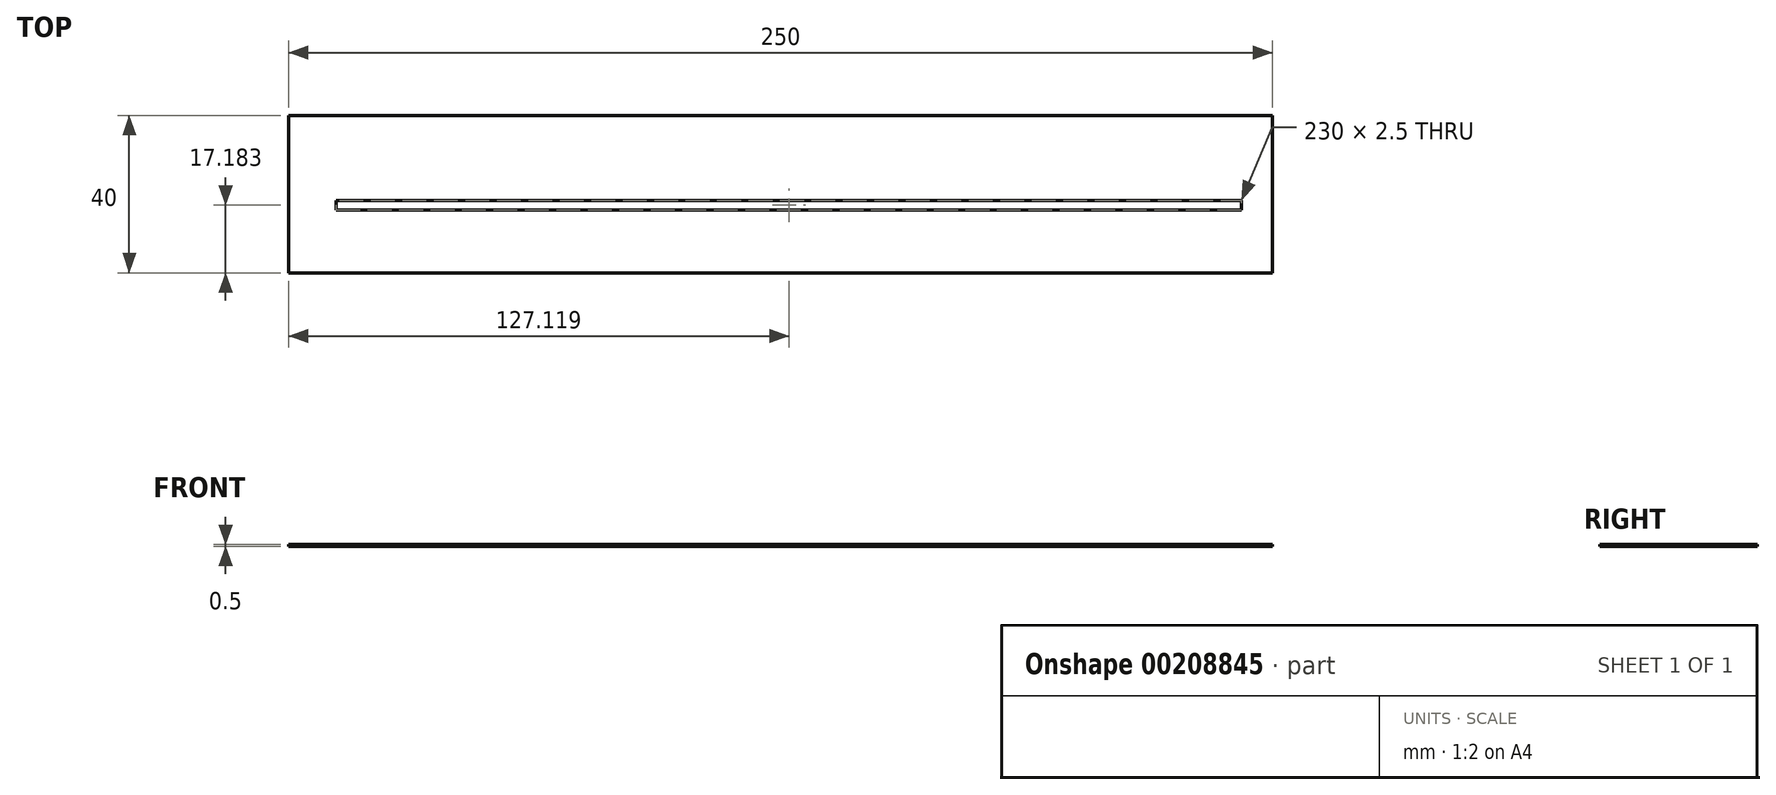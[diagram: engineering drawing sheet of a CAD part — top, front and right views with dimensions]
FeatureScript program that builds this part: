
annotation { "Feature Type Name" : "Feature", "Feature Type Description" : "" }
export const myFeature = defineFeature(function(context is Context, id is Id, definition is map)
    precondition{}
    {
        {
            var Q0;
            Q0=qCreatedBy(makeId("Top.planeOp"),FACE);
            var sketch = newSketch(context, id + "F0", { "sketchPlane" : qUnion([Q0])});
            skLineSegment(sketch, "E0.bottom", {"start": v(-125.07, 12.47) * mm, "end": v(124.93, 12.47) * mm});
            skLineSegment(sketch, "E0.top", {"start": v(-125.07, -27.53) * mm, "end": v(124.93, -27.53) * mm});
            skLineSegment(sketch, "E0.left", {"start": v(-125.07, 12.47) * mm, "end": v(-125.07, -27.53) * mm});
            skLineSegment(sketch, "E0.right", {"start": v(124.93, 12.47) * mm, "end": v(124.93, -27.53) * mm});
            skLineSegment(sketch, "E1.bottom", {"start": v(-112.95, -9.1) * mm, "end": v(117.05, -9.1) * mm});
            skLineSegment(sketch, "E1.top", {"start": v(-112.95, -11.6) * mm, "end": v(117.05, -11.6) * mm});
            skLineSegment(sketch, "E1.left", {"start": v(-112.95, -9.1) * mm, "end": v(-112.95, -11.6) * mm});
            skLineSegment(sketch, "E1.right", {"start": v(117.05, -9.1) * mm, "end": v(117.05, -11.6) * mm});
            skSolve(sketch);
        }
        {
            var Q0;
            Q0=makeQuery(id+"F0.imprint","IMPRINT",FACE,{"disambiguationData":[TD([[makeQuery(id+"F0.imprint","IMPRINT",EDGE,{"derivedFrom":sQuery(id+"F0.wireOp",EDGE,"E0.bottom")}),-1.0]])]});
            extrude(context, id + "F1", {"entities" : qUnion([Q0]), "depth" : 0.5 * mm});
        }
    });
